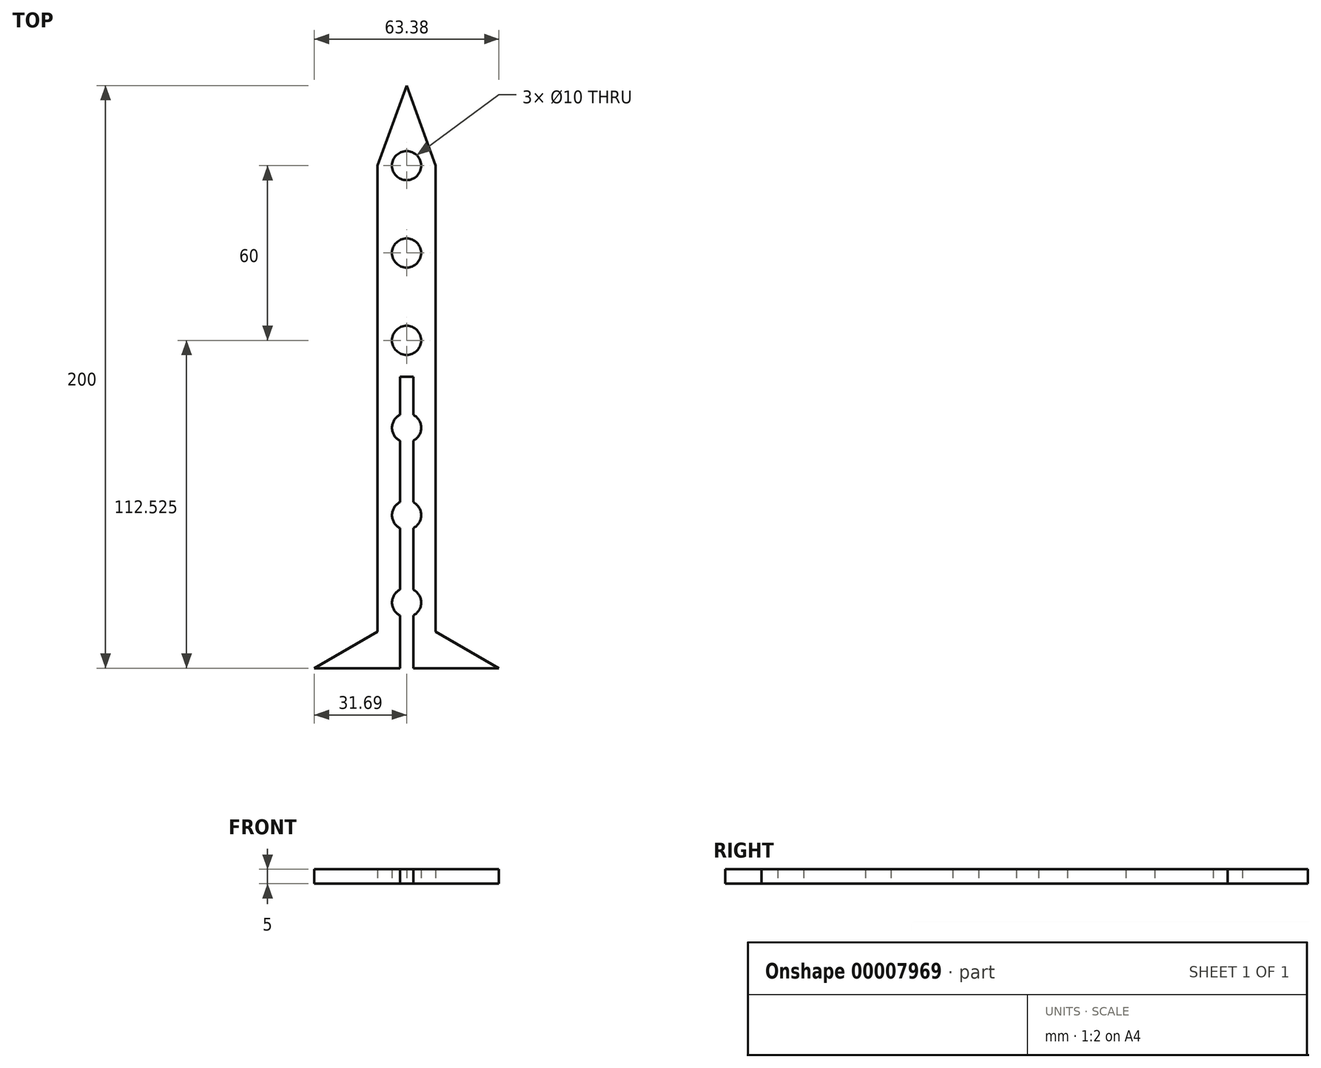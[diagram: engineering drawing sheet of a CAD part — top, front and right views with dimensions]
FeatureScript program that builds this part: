
annotation { "Feature Type Name" : "Feature", "Feature Type Description" : "" }
export const myFeature = defineFeature(function(context is Context, id is Id, definition is map)
    precondition{}
    {
        {
            var Q0;
            Q0=qCreatedBy(makeId("Top.planeOp"),FACE);
            var sketch = newSketch(context, id + "F0", { "sketchPlane" : qUnion([Q0])});
            skLineSegment(sketch, "E0.left", {"start": v(-10, -27.47) * mm, "end": v(-10, -187.47) * mm});
            skLineSegment(sketch, "E1", {"start": v(-10, -27.47) * mm, "end": v(0, 0) * mm});
            skLineSegment(sketch, "E2", {"start": v(-10, -187.47) * mm, "end": v(-31.7, -200) * mm});
            skLineSegment(sketch, "E3", {"start": v(-31.7, -200) * mm, "end": v(-2.3, -200) * mm});
            skLineSegment(sketch, "E4.0.MirrorCS", {"start": v(10, -27.47) * mm, "end": v(0, 0) * mm});
            skLineSegment(sketch, "E5.0.MirrorCS", {"start": v(10, -27.47) * mm, "end": v(10, -187.47) * mm});
            skLineSegment(sketch, "E6.0.MirrorCS", {"start": v(10, -187.47) * mm, "end": v(31.7, -200) * mm});
            skLineSegment(sketch, "E7.0.MirrorCS", {"start": v(31.7, -200) * mm, "end": v(2.3, -200) * mm});
            skCircle(sketch, "E8", {"center": v(0, -27.47) * mm, "radius": 5 * mm});
            skCircle(sketch, "E9.0.1.0", {"center": v(0, -57.47) * mm, "radius": 5 * mm});
            skCircle(sketch, "E9.0.2.0", {"center": v(0, -87.47) * mm, "radius": 5 * mm});
            skArc(sketch, "E9.0.3.0", {"start": v(-2.3, -113.04) * mm, "mid": v(-5, -117.47) * mm, "end": v(-2.3, -121.91) * mm});
            skArc(sketch, "E9.0.4.0", {"start": v(-2.3, -143.04) * mm, "mid": v(-5, -147.47) * mm, "end": v(-2.3, -151.91) * mm});
            skArc(sketch, "E9.0.5.0", {"start": v(-2.3, -173.04) * mm, "mid": v(-5, -177.47) * mm, "end": v(-2.3, -181.91) * mm});
            skLineSegment(sketch, "E9.direction1", {"start": v(0, -27.47) * mm, "end": v(35.48, -27.47) * mm, "construction": true});
            skLineSegment(sketch, "E9.direction2", {"start": v(0, -27.47) * mm, "end": v(0, -57.47) * mm, "construction": true});
            skLineSegment(sketch, "E10.top", {"start": v(2.3, -100) * mm, "end": v(-2.3, -100) * mm});
            skLineSegment(sketch, "E10.left", {"start": v(2.3, -200) * mm, "end": v(2.3, -181.91) * mm});
            skLineSegment(sketch, "E10.right", {"start": v(-2.3, -200) * mm, "end": v(-2.3, -181.91) * mm});
            skArc(sketch, "E11.trimOffspring", {"start": v(2.3, -121.91) * mm, "mid": v(5, -117.47) * mm, "end": v(2.3, -113.04) * mm});
            skLineSegment(sketch, "E12.trimOffspring", {"start": v(-2.3, -143.04) * mm, "end": v(-2.3, -121.91) * mm});
            skLineSegment(sketch, "E13.trimOffspring", {"start": v(2.3, -143.04) * mm, "end": v(2.3, -121.91) * mm});
            skLineSegment(sketch, "E14.trimOffspring", {"start": v(-2.3, -113.04) * mm, "end": v(-2.3, -100) * mm});
            skLineSegment(sketch, "E15.trimOffspring", {"start": v(2.3, -113.04) * mm, "end": v(2.3, -100) * mm});
            skArc(sketch, "E16.trimOffspring", {"start": v(2.3, -151.91) * mm, "mid": v(5, -147.47) * mm, "end": v(2.3, -143.04) * mm});
            skLineSegment(sketch, "E17.trimOffspring", {"start": v(2.3, -173.04) * mm, "end": v(2.3, -151.91) * mm});
            skLineSegment(sketch, "E18.trimOffspring", {"start": v(-2.3, -173.04) * mm, "end": v(-2.3, -151.91) * mm});
            skArc(sketch, "E19.trimOffspring", {"start": v(2.3, -181.91) * mm, "mid": v(5, -177.47) * mm, "end": v(2.3, -173.04) * mm});
            skPoint(sketch, "E20.orphan", {"position": v(0, -200) * mm});
            skSolve(sketch);
        }
        {
            var Q0;
            Q0 = qSketchRegion(id + "F0", true);
            extrude(context, id + "F1", {"entities" : qUnion([Q0]), "depth" : 5 * mm});
        }
    });
